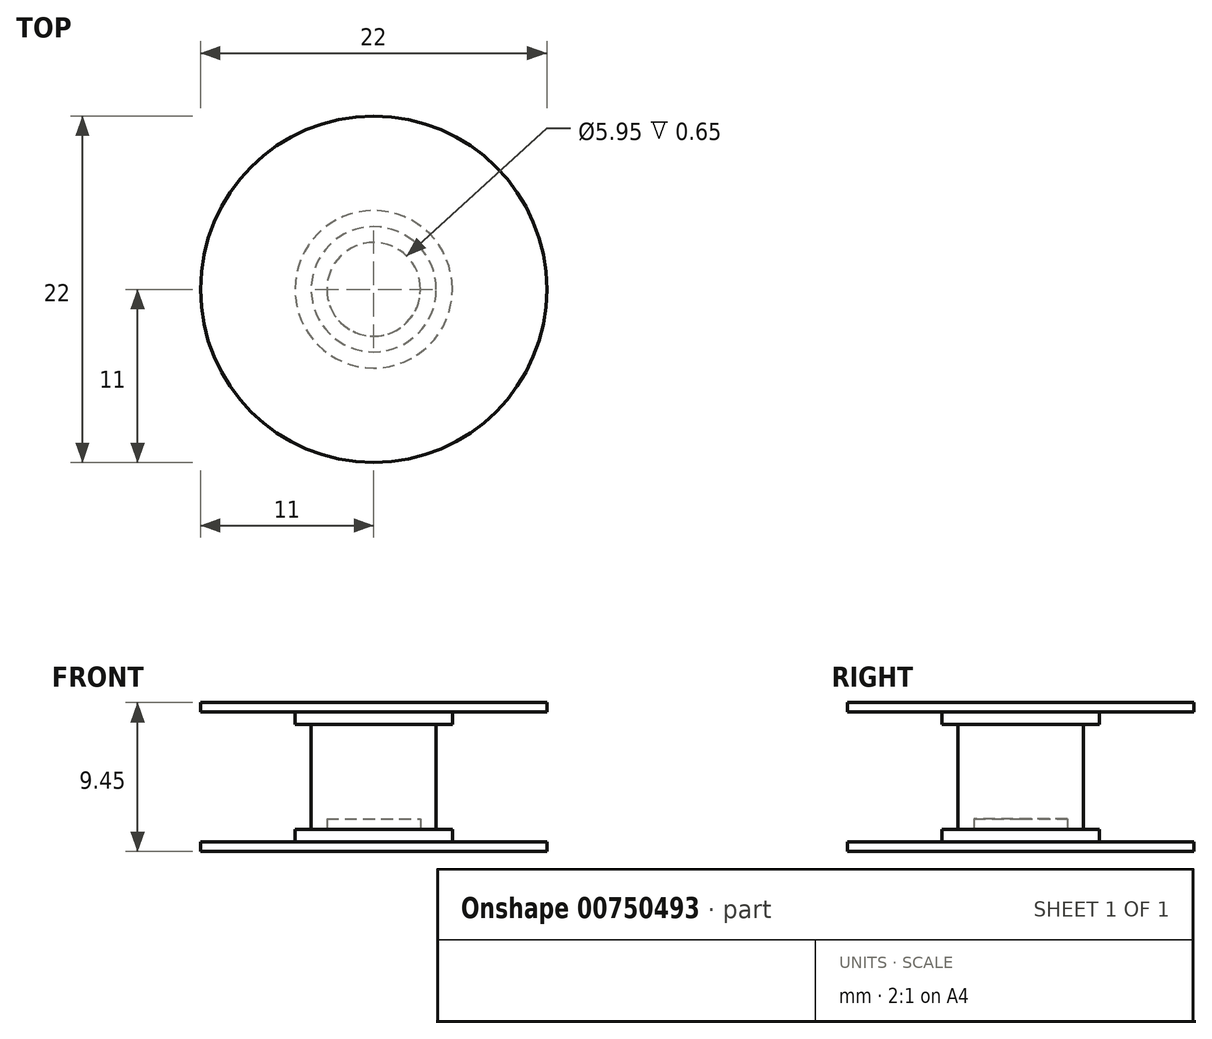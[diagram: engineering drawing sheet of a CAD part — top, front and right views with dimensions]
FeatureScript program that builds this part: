
annotation { "Feature Type Name" : "Feature", "Feature Type Description" : "" }
export const myFeature = defineFeature(function(context is Context, id is Id, definition is map)
    precondition{}
    {
        {
            var Q0;
            Q0=qCreatedBy(makeId("Front.planeOp"),FACE);
            var sketch = newSketch(context, id + "F0", { "sketchPlane" : qUnion([Q0])});
            skLineSegment(sketch, "E0.bottom", {"start": v(0, 0) * mm, "end": v(-5, 0) * mm});
            skLineSegment(sketch, "E0.top", {"start": v(0, 0.8) * mm, "end": v(-5, 0.8) * mm});
            skLineSegment(sketch, "E0.left", {"start": v(0, 0) * mm, "end": v(0, 0.8) * mm});
            skLineSegment(sketch, "E0.right", {"start": v(-5, 0) * mm, "end": v(-5, 0.8) * mm});
            skLineSegment(sketch, "E1.bottom", {"start": v(0, 0) * mm, "end": v(-11, 0) * mm});
            skLineSegment(sketch, "E1.left", {"start": v(0, 0) * mm, "end": v(0, -0.6) * mm});
            skLineSegment(sketch, "E1.right", {"start": v(-11, 0) * mm, "end": v(-11, -0.6) * mm});
            skLineSegment(sketch, "E2.top", {"start": v(0, -0.6) * mm, "end": v(-11, -0.6) * mm});
            skLineSegment(sketch, "E3.bottom", {"start": v(-11, -0.6) * mm, "end": v(-10.4, -0.6) * mm});
            skPoint(sketch, "E4", {"position": v(0, 4.12) * mm});
            skLineSegment(sketch, "E5", {"start": v(-14.4, 4.12) * mm, "end": v(14.37, 4.12) * mm, "construction": true});
            skLineSegment(sketch, "E6.MirrorCS", {"start": v(-11, 8.25) * mm, "end": v(-11, 8.85) * mm});
            skLineSegment(sketch, "E7.MirrorCS", {"start": v(0, 8.25) * mm, "end": v(-5, 8.25) * mm});
            skLineSegment(sketch, "E8.MirrorCS", {"start": v(0, 8.25) * mm, "end": v(-11, 8.25) * mm});
            skLineSegment(sketch, "E9.MirrorCS", {"start": v(0, 8.25) * mm, "end": v(0, 8.85) * mm});
            skLineSegment(sketch, "E10.MirrorCS", {"start": v(0, 8.85) * mm, "end": v(-11, 8.85) * mm});
            skLineSegment(sketch, "E11.MirrorCS", {"start": v(-11, 8.85) * mm, "end": v(-10.4, 8.85) * mm});
            skLineSegment(sketch, "E12.MirrorCS", {"start": v(0, 8.25) * mm, "end": v(0, 7.45) * mm});
            skLineSegment(sketch, "E13.MirrorCS", {"start": v(0, 7.45) * mm, "end": v(-5, 7.45) * mm});
            skLineSegment(sketch, "E14.MirrorCS", {"start": v(-5, 8.25) * mm, "end": v(-5, 7.45) * mm});
            skLineSegment(sketch, "E15", {"start": v(0, 13.43) * mm, "end": v(0, -5.6) * mm, "construction": true});
            skPoint(sketch, "E15.startSnap0", {"position": v(0, 8.55) * mm});
            skPoint(sketch, "E16.MirrorCS.start.orphan", {"position": v(-11, 9.45) * mm});
            skPoint(sketch, "E17.MirrorCS.start.orphan", {"position": v(-10.4, 9.45) * mm});
            skPoint(sketch, "E3.top.end.orphan", {"position": v(-10.4, -1.2) * mm});
            skSolve(sketch);
        }
        {
            var Q0;
            Q0=makeQuery(id+"F0.imprint","IMPRINT",FACE,{"disambiguationData":[TD([[makeQuery(id+"F0.imprint","IMPRINT",EDGE,{"derivedFrom":sQuery(id+"F0.wireOp",EDGE,"E0.bottom")}),-1.0]])]});
            var Q1;
            Q1=makeQuery(id+"F0.imprint","IMPRINT",FACE,{"disambiguationData":[TD([[makeQuery(id+"F0.imprint","IMPRINT",EDGE,{"derivedFrom":sQuery(id+"F0.wireOp",EDGE,"E0.bottom")}),1.0]])]});
            var Q2;
            Q2=makeQuery(id+"F0.imprint","IMPRINT",FACE,{"disambiguationData":[TD([[makeQuery(id+"F0.imprint","IMPRINT",EDGE,{"derivedFrom":sQuery(id+"F0.wireOp",EDGE,"E3.bottom")}),-1.0]])]});
            var Q3;
            Q3=sQuery(id+"F0.wireOp",EDGE,"E15");
            revolve(context, id + "F1", {"surfaceOperationType" : NewSurfaceOperationType.NEW, "entities" : qUnion([Q0, Q1, Q2]), "axis" : qUnion([Q3]), "revolveType" : RevolveType.FULL});
        }
        {
            var Q0;
            Q0=makeQuery(id+"F1.opRevolve","SWEPT_FACE",FACE,{"disambiguationData":[OSD([sQuery(id+"F0.wireOp",EDGE,"E0.top")])]});
            var sketch = newSketch(context, id + "F2", { "sketchPlane" : qUnion([Q0])});
            skCircle(sketch, "E18", {"center": v(0, 0) * mm, "radius": 3.98 * mm});
            skCircle(sketch, "E19", {"center": v(0, 0) * mm, "radius": 2.98 * mm});
            skSolve(sketch);
        }
        {
            var Q0;
            Q0=makeQuery(id+"F2.imprint","IMPRINT",FACE,{"disambiguationData":[TD([[makeQuery(id+"F2.imprint","IMPRINT",EDGE,{"derivedFrom":sQuery(id+"F2.wireOp",EDGE,"E18")}),1.0]])]});
            extrude(context, id + "F3", {"entities" : qUnion([Q0]), "operationType" : NewBodyOperationType.ADD, "depth" : 6.65 * mm, "offsetDistance" : 25 * mm});
        }
        {
            var Q0;
            {var subQ1=sQuery(id+"F0.wireOp",EDGE,"E6.MirrorCS");Q0=makeQuery(id+"F0.imprint","IMPRINT",FACE,{"disambiguationData":[TD([[makeQuery(id+"F0.imprint","IMPRINT",EDGE,{"derivedFrom":subQ1}),-1.0]])]});}
            var Q1;
            Q1=makeQuery(id+"F0.imprint","IMPRINT",FACE,{"disambiguationData":[TD([[makeQuery(id+"F0.imprint","IMPRINT",EDGE,{"derivedFrom":sQuery(id+"F0.wireOp",EDGE,"E7.MirrorCS")}),1.0]])]});
            var Q2;
            {var subQ0=sQuery(id+"F0.wireOp",EDGE,"E17.MirrorCS");Q2=makeQuery(id+"F0.imprint","IMPRINT",FACE,{"disambiguationData":[TD([[makeQuery(id+"F0.imprint","IMPRINT",EDGE,{"derivedFrom":subQ0}),1.0]])]});}
            var Q3;
            Q3=sQuery(id+"F0.wireOp",EDGE,"E15");
            revolve(context, id + "F4", {"surfaceOperationType" : NewSurfaceOperationType.NEW, "entities" : qUnion([Q0, Q1, Q2]), "axis" : qUnion([Q3]), "revolveType" : RevolveType.FULL});
        }
        {
            var Q0;
            Q0=makeQuery(id+"F4.opRevolve","SWEPT_FACE",FACE,{"disambiguationData":[OSD([sQuery(id+"F0.wireOp",EDGE,"E13.MirrorCS")])]});
            var sketch = newSketch(context, id + "F5", { "sketchPlane" : qUnion([Q0])});
            skCircle(sketch, "E20", {"center": v(0, 0) * mm, "radius": 2.98 * mm});
            skSolve(sketch);
        }
        {
            var Q0;
            Q0=makeQuery(id+"F5.imprint","IMPRINT",FACE,{"disambiguationData":[TD([[makeQuery(id+"F5.imprint","IMPRINT",EDGE,{"derivedFrom":sQuery(id+"F5.wireOp",EDGE,"E20")}),1.0]])]});
            extrude(context, id + "F6", {"entities" : qUnion([Q0]), "operationType" : NewBodyOperationType.ADD, "depth" : 6 * mm, "offsetDistance" : 25 * mm});
        }
    });
